# Revit family: DiLED Frame Prism - Generic
name_source: partatom
category: Lighting Fixtures
revit_build: Autodesk Revit Architecture 2014 (Build: 20140709_2115(x64)
units: mm (PartAtom-declared; Revit-internal decimal feet)

## types (4) — shared parameters
Apparent Load = 240 VA
ArticleNumber = See URL hyperlink
AssetType = Moveable/Fixed
BSAB 96 = SNB.2
BallastsCELMAEnergyEfficiencyIndex = Class A1/A2
CCSClassCode = UAC
CCSClassName = Belysningsarmatur
CCSTopnode = L
Clearance Zones = 60 mm  [stored 0.19685 ft]
Clearance Zones Visible = Yes
Colour = White
ControlGearPosition = Integrated
Description = 70-80-35 General Lighting Systems
DocumentReference = See URL hyperlink
Documentation = See URL hyperlink
Finish = Powder coated
Glass Thickness = 2 mm  [stored 0.00656168 ft]
H1 = 52 mm
H2 = 90 mm
HasProtectiveEarth = TRUE
IP_Code = IP20 (IP44 from below)
IfcExportAs = IfcLightFixtureType'
IfcExportType = NOTDEFINED'
InsulationStandardClass = Class 1
InternalFuse = Only required in emergency versions
LampColourRenderingIndex = Ra>80
LampType = LED
Light Source Definition (family) = Point+HemiSpherical
Light Source Symbol Size = 500 mm  [stored 1.64042 ft]
LightFixtureMountingType = Recessed
LightFixturePlacingType = Ceiling
LightSource = LED 3000K / 4000K
LuminairePowerFactor = >0,9
LuminaireType = Recessed Direct LED Luminaire
Manufacturer = Riegens A/S
ManufacturerURL = www.riegens.com
Material = Steel and Acrylic (PMMA)
NominalVoltage = 220-240V
OmniClass Number = 23.80.70.11
OmniClass Title = Luminaries for Internal Lighting
Optic = Anti-glare prismatic diffuser
PhaseReference = IEC recommendations
PhotometricPerformance = In accordance with BS EN 13032-1
ProductInformation = http://riegens.com
Shape = Square
URL = http://riegens.com
Uniclass 1.4 = JY73
Uniclass2 = Pr_70_70_49_43 Light-Emitting Diode (LED) Luminaires
Version = v.1.0

## per-type parameters (varying)
| type | BIMObjectName | Cassette | Cassette Depth | Cassette Width | Frame | Frame Depth | Frame Width | LampRating | Size | TotalWattage | Transformer | Transformer Offset 1 |
| DiLED Frame Prism 1200x300 T | DiLED Frame Prism 1200x300 T.rfa | <By Category> | 270 mm  [stored 0.885827 ft] | 1170 mm  [stored 3.83858 ft] | <By Category> | 295 mm  [stored 0.967848 ft] | 1195 mm  [stored 3.9206 ft] | 42W | 1200 x 300 mm | Max. 45W | <By Category> | 93 mm  [stored 0.305118 ft] |
| DiLED Frame Prism 300x300 T | DiLED Frame Prism 300x300 T.rfa | <By Category> | 270 mm  [stored 0.885827 ft] | 270 mm  [stored 0.885827 ft] | <By Category> | 295 mm  [stored 0.967848 ft] | 295 mm  [stored 0.967848 ft] | 12W | 300 x 300 mm | Max. 15W | <By Category> | 0 mm  [stored 0 ft] |
| DiLED Frame Prism 600x600 T | DiLED Frame Prism 600x600 T.rfa | Riegens_Steel_Powder coated white RAL901025 | 570 mm  [stored 1.87008 ft] | 570 mm  [stored 1.87008 ft] | Riegens_Steel_Powder coated white RAL901025 | 595 mm  [stored 1.9521 ft] | 595 mm  [stored 1.9521 ft] | 42W | 600 x 600 mm | Max. 45W | Riegens_Aluminum | 245 mm  [stored 0.803806 ft] |
| DiLED Frame Prism 625x625 T | DiLED Frame Prism 625x625 T.rfa | <By Category> | 600 mm | 600 mm | <By Category> | 620 mm  [stored 2.03412 ft] | 620 mm  [stored 2.03412 ft] | 42W | 625 x 625 mm | Max. 45W | <By Category> | 245 mm  [stored 0.803806 ft] |

note: column(s) folded — value = type name in every type: Model, ModelReference

note: [stored X ft] marks values corroborated as IEEE doubles in the binary element streams (Revit-internal decimal feet)

## geometry (parser evidence)
native form markers: Blend x81, Sweep x2
no freeform markers — native parametric forms only
